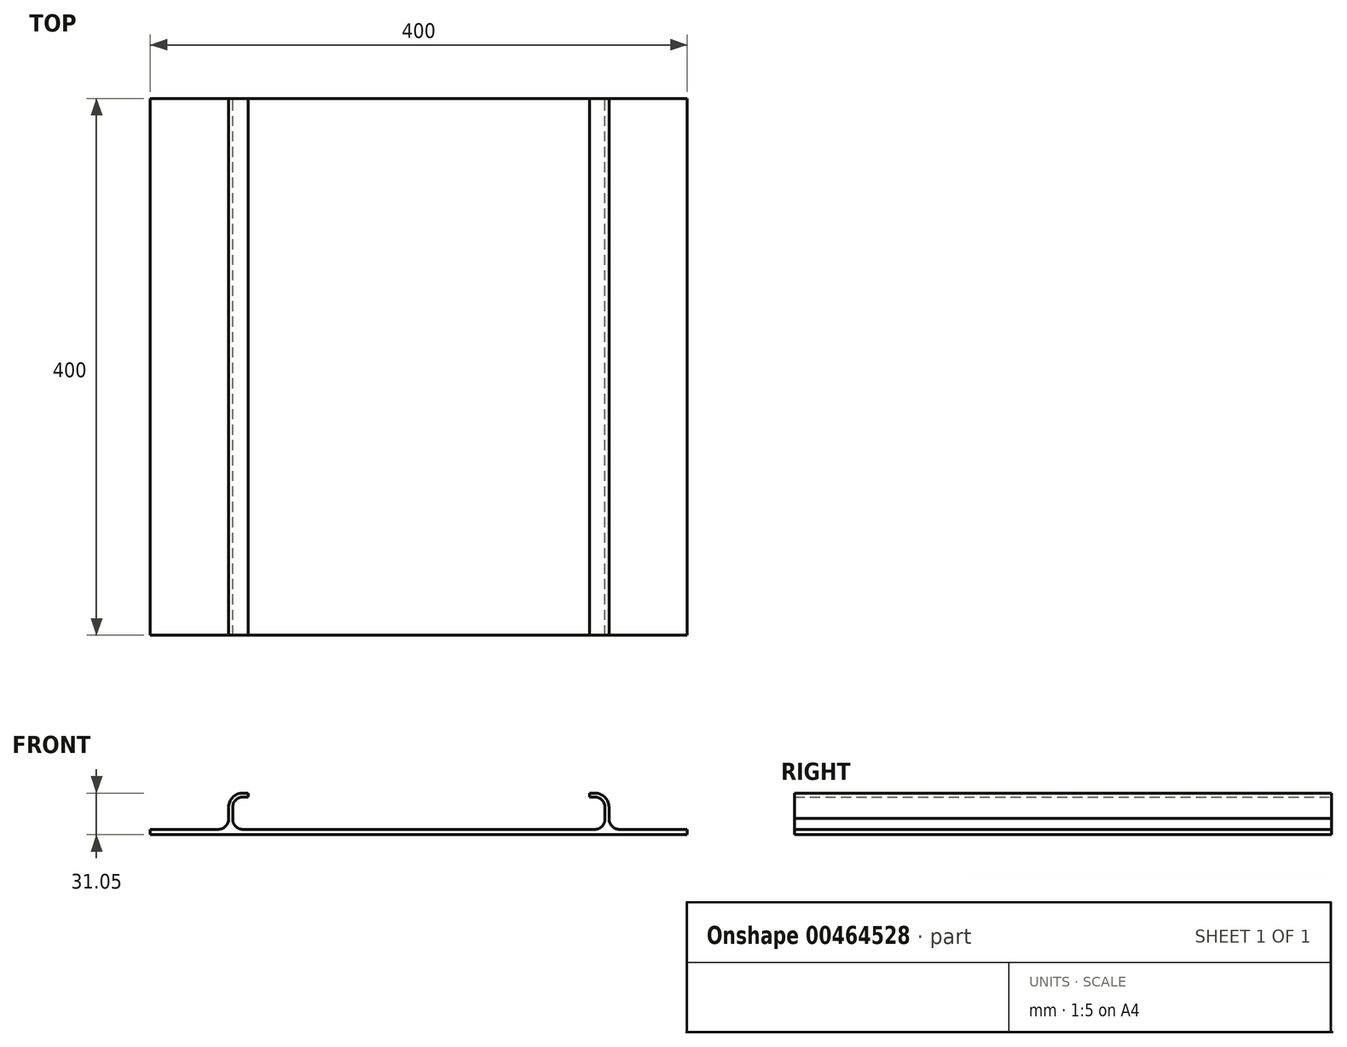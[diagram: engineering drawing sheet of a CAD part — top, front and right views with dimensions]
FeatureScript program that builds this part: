
annotation { "Feature Type Name" : "Feature", "Feature Type Description" : "" }
export const myFeature = defineFeature(function(context is Context, id is Id, definition is map)
    precondition{}
    {
        {
            var Q0;
            Q0=qCreatedBy(makeId("Front.planeOp"),FACE);
            var sketch = newSketch(context, id + "F0", { "sketchPlane" : qUnion([Q0])});
            skLineSegment(sketch, "E0", {"start": v(-140.82, -56.6) * mm, "end": v(-50.82, -56.6) * mm});
            skLineSegment(sketch, "E1.MirrorCS", {"start": v(-148.32, -48.59) * mm, "end": v(-148.32, -40.04) * mm});
            skLineSegment(sketch, "E2.MirrorCS", {"start": v(-140.82, -32.54) * mm, "end": v(-136.72, -32.54) * mm});
            skArc(sketch, "E3.MirrorCS", {"start": v(-140.82, -56.6) * mm, "mid": v(-146.3, -54.22) * mm, "end": v(-148.32, -48.59) * mm});
            skArc(sketch, "E4.MirrorCS", {"start": v(-148.32, -40.04) * mm, "mid": v(-146.12, -34.74) * mm, "end": v(-140.82, -32.54) * mm});
            skLineSegment(sketch, "E5.0", {"start": v(-140.82, -29.54) * mm, "end": v(-136.72, -29.54) * mm});
            skArc(sketch, "E5.1", {"start": v(-151.32, -40.04) * mm, "mid": v(-148.24, -32.62) * mm, "end": v(-140.82, -29.54) * mm});
            skLineSegment(sketch, "E5.2", {"start": v(-151.32, -48.5) * mm, "end": v(-151.32, -40.04) * mm});
            skArc(sketch, "E5.3", {"start": v(-151.33, -48.81) * mm, "mid": v(-151.32, -48.65) * mm, "end": v(-151.32, -48.5) * mm});
            skLineSegment(sketch, "E6", {"start": v(-103.56, -56.6) * mm, "end": v(-140.85, -56.6) * mm});
            skLineSegment(sketch, "E7.trimOffspring", {"start": v(-159.33, -56.6) * mm, "end": v(-209.67, -56.6) * mm});
            skLineSegment(sketch, "E8", {"start": v(-209.67, -56.6) * mm, "end": v(-209.67, -60.6) * mm});
            skLineSegment(sketch, "E9", {"start": v(-209.67, -60.6) * mm, "end": v(-9.67, -60.6) * mm});
            skArc(sketch, "E10.filletArc", {"start": v(-159.33, -56.6) * mm, "mid": v(-153.75, -54.33) * mm, "end": v(-151.33, -48.81) * mm});
            skLineSegment(sketch, "E11", {"start": v(-59.15, -56.6) * mm, "end": v(-9.67, -56.6) * mm});
            skArc(sketch, "E12.MirrorCS", {"start": v(132, -48.81) * mm, "mid": v(132, -48.65) * mm, "end": v(131.99, -48.5) * mm});
            skLineSegment(sketch, "E13.MirrorCS", {"start": v(128.99, -48.59) * mm, "end": v(128.99, -40.04) * mm});
            skLineSegment(sketch, "E14.MirrorCS", {"start": v(121.49, -32.54) * mm, "end": v(117.4, -32.54) * mm});
            skLineSegment(sketch, "E15.MirrorCS", {"start": v(190.33, -56.6) * mm, "end": v(190.33, -60.6) * mm});
            skLineSegment(sketch, "E16.MirrorCS", {"start": v(131.99, -48.5) * mm, "end": v(131.99, -40.04) * mm});
            skLineSegment(sketch, "E17.MirrorCS", {"start": v(121.49, -29.54) * mm, "end": v(117.4, -29.54) * mm});
            skArc(sketch, "E18.MirrorCS", {"start": v(121.49, -56.6) * mm, "mid": v(126.98, -54.22) * mm, "end": v(128.99, -48.59) * mm});
            skArc(sketch, "E19.MirrorCS", {"start": v(128.99, -40.04) * mm, "mid": v(126.8, -34.74) * mm, "end": v(121.49, -32.54) * mm});
            skLineSegment(sketch, "E20.MirrorCS", {"start": v(84.23, -56.6) * mm, "end": v(121.52, -56.6) * mm});
            skLineSegment(sketch, "E21.MirrorCS", {"start": v(121.49, -56.6) * mm, "end": v(31.49, -56.6) * mm});
            skLineSegment(sketch, "E22.MirrorCS", {"start": v(140, -56.6) * mm, "end": v(190.33, -56.6) * mm});
            skArc(sketch, "E23.MirrorCS", {"start": v(140, -56.6) * mm, "mid": v(134.42, -54.33) * mm, "end": v(132, -48.81) * mm});
            skArc(sketch, "E24.MirrorCS", {"start": v(131.99, -40.04) * mm, "mid": v(128.91, -32.62) * mm, "end": v(121.49, -29.54) * mm});
            skLineSegment(sketch, "E25", {"start": v(31.49, -56.6) * mm, "end": v(-9.67, -56.6) * mm});
            skLineSegment(sketch, "E26", {"start": v(190.33, -60.6) * mm, "end": v(-9.67, -60.6) * mm});
            skLineSegment(sketch, "E27", {"start": v(-136.72, -29.54) * mm, "end": v(-136.72, -32.54) * mm});
            skLineSegment(sketch, "E28", {"start": v(117.4, -29.54) * mm, "end": v(117.4, -32.54) * mm});
            skSolve(sketch);
        }
        {
            var Q0;
            Q0 = qSketchRegion(id + "F0", true);
            extrude(context, id + "F1", {"entities" : qUnion([Q0]), "depth" : 400 * mm});
        }
    });
